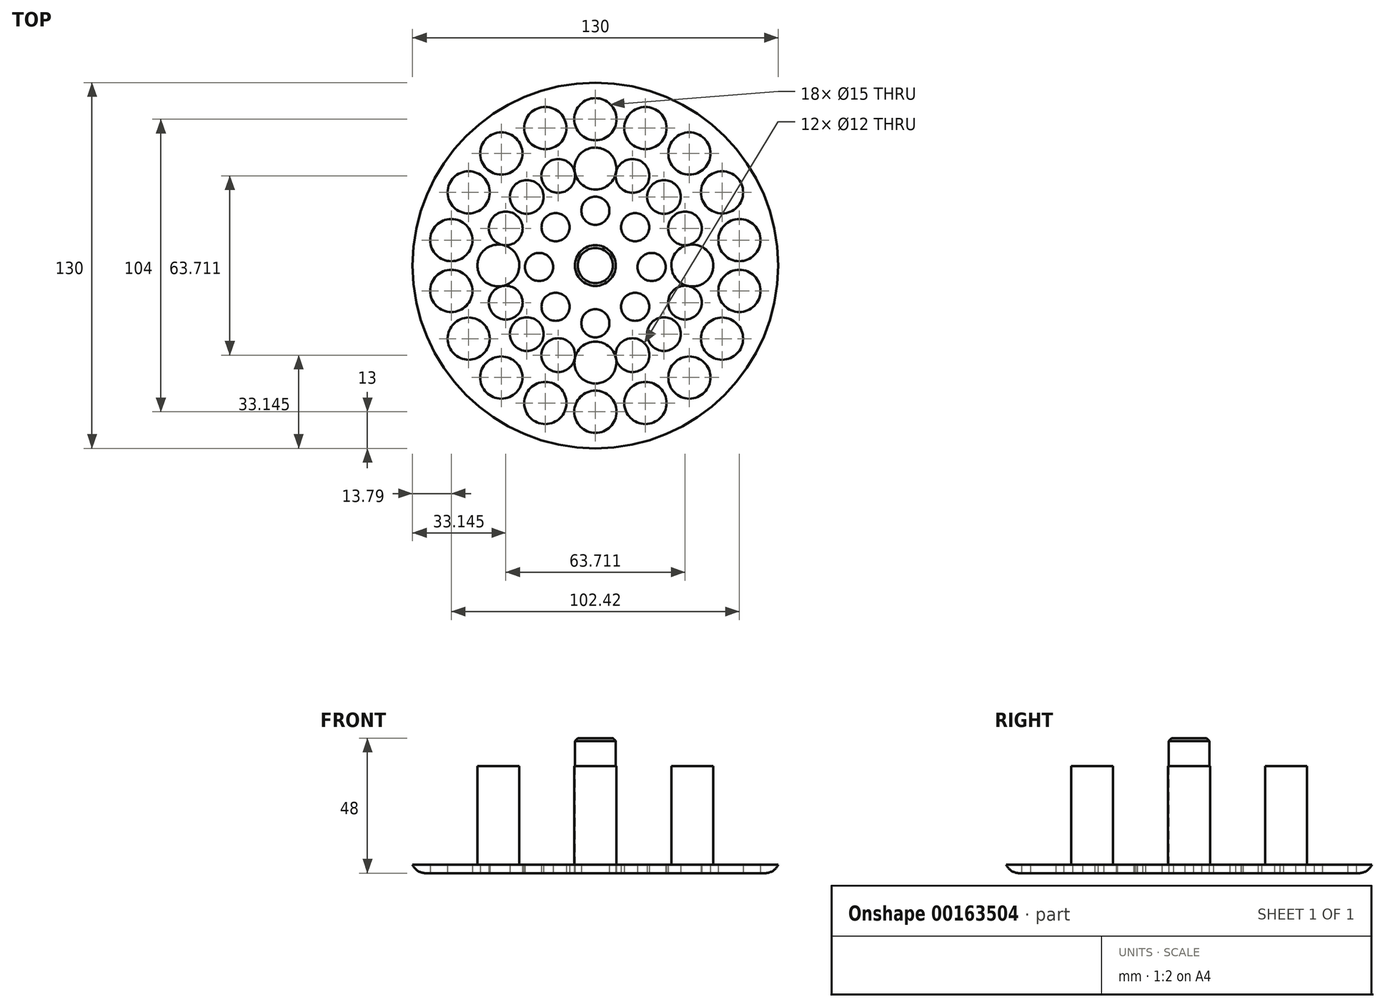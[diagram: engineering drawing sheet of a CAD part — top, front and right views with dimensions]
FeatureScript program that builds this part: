
annotation { "Feature Type Name" : "Feature", "Feature Type Description" : "" }
export const myFeature = defineFeature(function(context is Context, id is Id, definition is map)
    precondition{}
    {
        {
            var Q0;
            Q0=qCreatedBy(makeId("Top.planeOp"),FACE);
            var sketch = newSketch(context, id + "F0", { "sketchPlane" : qUnion([Q0])});
            skCircle(sketch, "E0", {"center": v(0, 0) * mm, "radius": 65 * mm});
            skCircle(sketch, "E1", {"center": v(0, 19.48) * mm, "radius": 5 * mm});
            skCircle(sketch, "E2.1.0", {"center": v(-14.14, 13.62) * mm, "radius": 5 * mm});
            skCircle(sketch, "E2.2.0", {"center": v(-20, -0.52) * mm, "radius": 5 * mm});
            skCircle(sketch, "E2.3.0", {"center": v(-14.14, -14.66) * mm, "radius": 5 * mm});
            skCircle(sketch, "E2.4.0", {"center": v(0, -20.52) * mm, "radius": 5 * mm});
            skCircle(sketch, "E2.5.0", {"center": v(14.14, -14.66) * mm, "radius": 5 * mm});
            skCircle(sketch, "E2.6.0", {"center": v(20, -0.52) * mm, "radius": 5 * mm});
            skCircle(sketch, "E2.7.0", {"center": v(14.14, 13.62) * mm, "radius": 5 * mm});
            skPoint(sketch, "E2.center", {"position": v(0, -0.52) * mm});
            skCircle(sketch, "E3", {"center": v(0, 34.48) * mm, "radius": 6 * mm});
            skCircle(sketch, "E4.1.0", {"center": v(-13.2, 31.86) * mm, "radius": 6 * mm});
            skCircle(sketch, "E4.2.0", {"center": v(-24.38, 24.38) * mm, "radius": 6 * mm});
            skCircle(sketch, "E4.3.0", {"center": v(-31.86, 13.2) * mm, "radius": 6 * mm});
            skCircle(sketch, "E4.4.0", {"center": v(-34.48, 0) * mm, "radius": 6 * mm});
            skCircle(sketch, "E4.5.0", {"center": v(-31.86, -13.2) * mm, "radius": 6 * mm});
            skCircle(sketch, "E4.6.0", {"center": v(-24.38, -24.38) * mm, "radius": 6 * mm});
            skCircle(sketch, "E4.7.0", {"center": v(-13.2, -31.86) * mm, "radius": 6 * mm});
            skCircle(sketch, "E4.8.0", {"center": v(0, -34.48) * mm, "radius": 6 * mm});
            skCircle(sketch, "E4.9.0", {"center": v(13.2, -31.86) * mm, "radius": 6 * mm});
            skCircle(sketch, "E4.10.0", {"center": v(24.38, -24.38) * mm, "radius": 6 * mm});
            skCircle(sketch, "E4.11.0", {"center": v(31.86, -13.2) * mm, "radius": 6 * mm});
            skCircle(sketch, "E4.12.0", {"center": v(34.48, 0) * mm, "radius": 6 * mm});
            skCircle(sketch, "E4.13.0", {"center": v(31.86, 13.2) * mm, "radius": 6 * mm});
            skCircle(sketch, "E4.14.0", {"center": v(24.38, 24.38) * mm, "radius": 6 * mm});
            skCircle(sketch, "E4.15.0", {"center": v(13.2, 31.86) * mm, "radius": 6 * mm});
            skCircle(sketch, "E5", {"center": v(0, 52) * mm, "radius": 7.5 * mm});
            skCircle(sketch, "E6.1.0", {"center": v(-17.79, 48.86) * mm, "radius": 7.5 * mm});
            skCircle(sketch, "E6.2.0", {"center": v(-33.42, 39.83) * mm, "radius": 7.5 * mm});
            skCircle(sketch, "E6.3.0", {"center": v(-45.03, 26) * mm, "radius": 7.5 * mm});
            skCircle(sketch, "E6.4.0", {"center": v(-51.21, 9.03) * mm, "radius": 7.5 * mm});
            skCircle(sketch, "E6.5.0", {"center": v(-51.21, -9.03) * mm, "radius": 7.5 * mm});
            skCircle(sketch, "E6.6.0", {"center": v(-45.03, -26) * mm, "radius": 7.5 * mm});
            skCircle(sketch, "E6.7.0", {"center": v(-33.42, -39.83) * mm, "radius": 7.5 * mm});
            skCircle(sketch, "E6.8.0", {"center": v(-17.79, -48.86) * mm, "radius": 7.5 * mm});
            skCircle(sketch, "E6.9.0", {"center": v(0, -52) * mm, "radius": 7.5 * mm});
            skCircle(sketch, "E6.10.0", {"center": v(17.79, -48.86) * mm, "radius": 7.5 * mm});
            skCircle(sketch, "E6.11.0", {"center": v(33.42, -39.83) * mm, "radius": 7.5 * mm});
            skCircle(sketch, "E6.12.0", {"center": v(45.03, -26) * mm, "radius": 7.5 * mm});
            skCircle(sketch, "E6.13.0", {"center": v(51.21, -9.03) * mm, "radius": 7.5 * mm});
            skCircle(sketch, "E6.14.0", {"center": v(51.21, 9.03) * mm, "radius": 7.5 * mm});
            skCircle(sketch, "E6.15.0", {"center": v(45.03, 26) * mm, "radius": 7.5 * mm});
            skCircle(sketch, "E6.16.0", {"center": v(33.42, 39.83) * mm, "radius": 7.5 * mm});
            skCircle(sketch, "E6.17.0", {"center": v(17.79, 48.86) * mm, "radius": 7.5 * mm});
            skSolve(sketch);
        }
        {
            var Q0;
            Q0=makeQuery(id+"F0.imprint","IMPRINT",FACE,{"disambiguationData":[TD([[makeQuery(id+"F0.imprint","IMPRINT",EDGE,{"derivedFrom":sQuery(id+"F0.wireOp",EDGE,"E0")}),1.0]])]});
            extrude(context, id + "F1", {"entities" : qUnion([Q0]), "depth" : 3 * mm});
        }
        {
            var Q0;
            Q0=makeQuery(id+"F1.opExtrude","CAP_FACE",FACE,{"disambiguationData":[OSD([sQuery(id+"F0.wireOp",EDGE,"E0"),sQuery(id+"F0.wireOp",EDGE,"E1"),sQuery(id+"F0.wireOp",EDGE,"E2.1.0"),sQuery(id+"F0.wireOp",EDGE,"E2.2.0"),sQuery(id+"F0.wireOp",EDGE,"E2.3.0"),sQuery(id+"F0.wireOp",EDGE,"E2.4.0"),sQuery(id+"F0.wireOp",EDGE,"E2.5.0"),sQuery(id+"F0.wireOp",EDGE,"E2.6.0"),sQuery(id+"F0.wireOp",EDGE,"E2.7.0"),sQuery(id+"F0.wireOp",EDGE,"E3"),sQuery(id+"F0.wireOp",EDGE,"E4.1.0"),sQuery(id+"F0.wireOp",EDGE,"E4.2.0"),sQuery(id+"F0.wireOp",EDGE,"E4.3.0"),sQuery(id+"F0.wireOp",EDGE,"E4.4.0"),sQuery(id+"F0.wireOp",EDGE,"E4.5.0"),sQuery(id+"F0.wireOp",EDGE,"E4.6.0"),sQuery(id+"F0.wireOp",EDGE,"E4.7.0"),sQuery(id+"F0.wireOp",EDGE,"E4.8.0"),sQuery(id+"F0.wireOp",EDGE,"E4.9.0"),sQuery(id+"F0.wireOp",EDGE,"E4.10.0"),sQuery(id+"F0.wireOp",EDGE,"E4.11.0"),sQuery(id+"F0.wireOp",EDGE,"E4.12.0"),sQuery(id+"F0.wireOp",EDGE,"E4.13.0"),sQuery(id+"F0.wireOp",EDGE,"E4.14.0"),sQuery(id+"F0.wireOp",EDGE,"E4.15.0"),sQuery(id+"F0.wireOp",EDGE,"E5"),sQuery(id+"F0.wireOp",EDGE,"E6.1.0"),sQuery(id+"F0.wireOp",EDGE,"E6.2.0"),sQuery(id+"F0.wireOp",EDGE,"E6.3.0"),sQuery(id+"F0.wireOp",EDGE,"E6.4.0"),sQuery(id+"F0.wireOp",EDGE,"E6.5.0"),sQuery(id+"F0.wireOp",EDGE,"E6.6.0"),sQuery(id+"F0.wireOp",EDGE,"E6.7.0"),sQuery(id+"F0.wireOp",EDGE,"E6.8.0"),sQuery(id+"F0.wireOp",EDGE,"E6.9.0"),sQuery(id+"F0.wireOp",EDGE,"E6.10.0"),sQuery(id+"F0.wireOp",EDGE,"E6.11.0"),sQuery(id+"F0.wireOp",EDGE,"E6.12.0"),sQuery(id+"F0.wireOp",EDGE,"E6.13.0"),sQuery(id+"F0.wireOp",EDGE,"E6.14.0"),sQuery(id+"F0.wireOp",EDGE,"E6.15.0"),sQuery(id+"F0.wireOp",EDGE,"E6.16.0"),sQuery(id+"F0.wireOp",EDGE,"E6.17.0")])],"isStart":false});
            var sketch = newSketch(context, id + "F2", { "sketchPlane" : qUnion([Q0])});
            skCircle(sketch, "E7", {"center": v(0, 0) * mm, "radius": 7.25 * mm});
            skCircle(sketch, "E8", {"center": v(-24.97, 0) * mm, "radius": 1.76 * mm});
            skSolve(sketch);
        }
        {
            var Q0;
            Q0=makeQuery(id+"F2.imprint","IMPRINT",FACE,{"disambiguationData":[TD([[makeQuery(id+"F2.imprint","IMPRINT",EDGE,{"derivedFrom":sQuery(id+"F2.wireOp",EDGE,"E7")}),1.0]])]});
            extrude(context, id + "F3", {"entities" : qUnion([Q0]), "operationType" : NewBodyOperationType.ADD, "depth" : 45 * mm});
        }
        {
            var Q0;
            Q0=makeQuery(id+"F3.opExtrude","CAP_EDGE",EDGE,{"disambiguationData":[OSD([sQuery(id+"F2.wireOp",EDGE,"E7")])],"isStart":false});
            chamfer(context, id + "F4", {"entities" : qUnion([Q0]), "width" : 1 * mm, "tangentPropagation" : true});
        }
        {
            var Q0;
            Q0=makeQuery(id+"F1.opExtrude","CAP_FACE",FACE,{"disambiguationData":[OSD([sQuery(id+"F0.wireOp",EDGE,"E0"),sQuery(id+"F0.wireOp",EDGE,"E1"),sQuery(id+"F0.wireOp",EDGE,"E2.1.0"),sQuery(id+"F0.wireOp",EDGE,"E2.2.0"),sQuery(id+"F0.wireOp",EDGE,"E2.3.0"),sQuery(id+"F0.wireOp",EDGE,"E2.4.0"),sQuery(id+"F0.wireOp",EDGE,"E2.5.0"),sQuery(id+"F0.wireOp",EDGE,"E2.6.0"),sQuery(id+"F0.wireOp",EDGE,"E2.7.0"),sQuery(id+"F0.wireOp",EDGE,"E3"),sQuery(id+"F0.wireOp",EDGE,"E4.1.0"),sQuery(id+"F0.wireOp",EDGE,"E4.2.0"),sQuery(id+"F0.wireOp",EDGE,"E4.3.0"),sQuery(id+"F0.wireOp",EDGE,"E4.4.0"),sQuery(id+"F0.wireOp",EDGE,"E4.5.0"),sQuery(id+"F0.wireOp",EDGE,"E4.6.0"),sQuery(id+"F0.wireOp",EDGE,"E4.7.0"),sQuery(id+"F0.wireOp",EDGE,"E4.8.0"),sQuery(id+"F0.wireOp",EDGE,"E4.9.0"),sQuery(id+"F0.wireOp",EDGE,"E4.10.0"),sQuery(id+"F0.wireOp",EDGE,"E4.11.0"),sQuery(id+"F0.wireOp",EDGE,"E4.12.0"),sQuery(id+"F0.wireOp",EDGE,"E4.13.0"),sQuery(id+"F0.wireOp",EDGE,"E4.14.0"),sQuery(id+"F0.wireOp",EDGE,"E4.15.0"),sQuery(id+"F0.wireOp",EDGE,"E5"),sQuery(id+"F0.wireOp",EDGE,"E6.1.0"),sQuery(id+"F0.wireOp",EDGE,"E6.2.0"),sQuery(id+"F0.wireOp",EDGE,"E6.3.0"),sQuery(id+"F0.wireOp",EDGE,"E6.4.0"),sQuery(id+"F0.wireOp",EDGE,"E6.5.0"),sQuery(id+"F0.wireOp",EDGE,"E6.6.0"),sQuery(id+"F0.wireOp",EDGE,"E6.7.0"),sQuery(id+"F0.wireOp",EDGE,"E6.8.0"),sQuery(id+"F0.wireOp",EDGE,"E6.9.0"),sQuery(id+"F0.wireOp",EDGE,"E6.10.0"),sQuery(id+"F0.wireOp",EDGE,"E6.11.0"),sQuery(id+"F0.wireOp",EDGE,"E6.12.0"),sQuery(id+"F0.wireOp",EDGE,"E6.13.0"),sQuery(id+"F0.wireOp",EDGE,"E6.14.0"),sQuery(id+"F0.wireOp",EDGE,"E6.15.0"),sQuery(id+"F0.wireOp",EDGE,"E6.16.0"),sQuery(id+"F0.wireOp",EDGE,"E6.17.0")])],"isStart":false});
            var sketch = newSketch(context, id + "F5", { "sketchPlane" : qUnion([Q0])});
            skCircle(sketch, "E9", {"center": v(0, 34.48) * mm, "radius": 7.45 * mm});
            skCircle(sketch, "E10.1.0", {"center": v(-34.48, 0) * mm, "radius": 7.45 * mm});
            skCircle(sketch, "E10.2.0", {"center": v(0, -34.48) * mm, "radius": 7.45 * mm});
            skCircle(sketch, "E10.3.0", {"center": v(34.48, 0) * mm, "radius": 7.45 * mm});
            skPoint(sketch, "E10.center", {"position": v(0, 0) * mm});
            skSolve(sketch);
        }
        {
            var Q0;
            Q0=makeQuery(id+"F5.imprint","IMPRINT",FACE,{"disambiguationData":[TD([[makeQuery(id+"F5.imprint","IMPRINT",EDGE,{"derivedFrom":makeQuery(id+"F1.opExtrude","CAP_EDGE",EDGE,{"disambiguationData":[OSD([sQuery(id+"F0.wireOp",EDGE,"E4.4.0")])],"isStart":false})}),1.0]])]});
            var Q1;
            Q1=makeQuery(id+"F5.imprint","IMPRINT",FACE,{"disambiguationData":[TD([[makeQuery(id+"F5.imprint","IMPRINT",EDGE,{"derivedFrom":makeQuery(id+"F1.opExtrude","CAP_EDGE",EDGE,{"disambiguationData":[OSD([sQuery(id+"F0.wireOp",EDGE,"E4.8.0")])],"isStart":false})}),1.0]])]});
            var Q2;
            Q2=makeQuery(id+"F5.imprint","IMPRINT",FACE,{"disambiguationData":[TD([[makeQuery(id+"F5.imprint","IMPRINT",EDGE,{"derivedFrom":makeQuery(id+"F1.opExtrude","CAP_EDGE",EDGE,{"disambiguationData":[OSD([sQuery(id+"F0.wireOp",EDGE,"E4.12.0")])],"isStart":false})}),1.0]])]});
            var Q3;
            Q3=makeQuery(id+"F5.imprint","IMPRINT",FACE,{"disambiguationData":[TD([[makeQuery(id+"F5.imprint","IMPRINT",EDGE,{"derivedFrom":makeQuery(id+"F1.opExtrude","CAP_EDGE",EDGE,{"disambiguationData":[OSD([sQuery(id+"F0.wireOp",EDGE,"E3")])],"isStart":false})}),-1.0]])]});
            var Q4;
            Q4=makeQuery(id+"F5.imprint","IMPRINT",FACE,{"disambiguationData":[TD([[makeQuery(id+"F5.imprint","IMPRINT",EDGE,{"derivedFrom":makeQuery(id+"F1.opExtrude","CAP_EDGE",EDGE,{"disambiguationData":[OSD([sQuery(id+"F0.wireOp",EDGE,"E4.4.0")])],"isStart":false})}),-1.0]])]});
            var Q5;
            Q5=makeQuery(id+"F5.imprint","IMPRINT",FACE,{"disambiguationData":[TD([[makeQuery(id+"F5.imprint","IMPRINT",EDGE,{"derivedFrom":makeQuery(id+"F1.opExtrude","CAP_EDGE",EDGE,{"disambiguationData":[OSD([sQuery(id+"F0.wireOp",EDGE,"E4.8.0")])],"isStart":false})}),-1.0]])]});
            var Q6;
            Q6=makeQuery(id+"F5.imprint","IMPRINT",FACE,{"disambiguationData":[TD([[makeQuery(id+"F5.imprint","IMPRINT",EDGE,{"derivedFrom":makeQuery(id+"F1.opExtrude","CAP_EDGE",EDGE,{"disambiguationData":[OSD([sQuery(id+"F0.wireOp",EDGE,"E4.12.0")])],"isStart":false})}),-1.0]])]});
            var Q7;
            Q7=makeQuery(id+"F5.imprint","IMPRINT",FACE,{"disambiguationData":[TD([[makeQuery(id+"F5.imprint","IMPRINT",EDGE,{"derivedFrom":makeQuery(id+"F1.opExtrude","CAP_EDGE",EDGE,{"disambiguationData":[OSD([sQuery(id+"F0.wireOp",EDGE,"E3")])],"isStart":false})}),1.0]])]});
            extrude(context, id + "F6", {"entities" : qUnion([Q0, Q1, Q2, Q3, Q4, Q5, Q6, Q7]), "operationType" : NewBodyOperationType.ADD, "depth" : 35 * mm});
        }
        {
            var Q0;
            Q0=makeQuery(id+"F6.opExtrude","CAP_FACE",FACE,{"disambiguationData":[OSD([sQuery(id+"F5.wireOp",EDGE,"E10.1.0")])],"isStart":true});
            var Q1;
            Q1=makeQuery(id+"F6.opExtrude","CAP_FACE",FACE,{"disambiguationData":[OSD([sQuery(id+"F5.wireOp",EDGE,"E10.2.0")])],"isStart":true});
            var Q2;
            Q2=makeQuery(id+"F6.opExtrude","CAP_FACE",FACE,{"disambiguationData":[OSD([sQuery(id+"F5.wireOp",EDGE,"E10.3.0")])],"isStart":true});
            var Q3;
            Q3=makeQuery(id+"F6.opExtrude","CAP_FACE",FACE,{"disambiguationData":[OSD([sQuery(id+"F5.wireOp",EDGE,"E9")])],"isStart":true});
            var Q4;
            Q4=makeQuery(id+"F1.opExtrude","CAP_FACE",FACE,{"disambiguationData":[OSD([sQuery(id+"F0.wireOp",EDGE,"E0"),sQuery(id+"F0.wireOp",EDGE,"E1"),sQuery(id+"F0.wireOp",EDGE,"E2.1.0"),sQuery(id+"F0.wireOp",EDGE,"E2.2.0"),sQuery(id+"F0.wireOp",EDGE,"E2.3.0"),sQuery(id+"F0.wireOp",EDGE,"E2.4.0"),sQuery(id+"F0.wireOp",EDGE,"E2.5.0"),sQuery(id+"F0.wireOp",EDGE,"E2.6.0"),sQuery(id+"F0.wireOp",EDGE,"E2.7.0"),sQuery(id+"F0.wireOp",EDGE,"E3"),sQuery(id+"F0.wireOp",EDGE,"E4.1.0"),sQuery(id+"F0.wireOp",EDGE,"E4.2.0"),sQuery(id+"F0.wireOp",EDGE,"E4.3.0"),sQuery(id+"F0.wireOp",EDGE,"E4.4.0"),sQuery(id+"F0.wireOp",EDGE,"E4.5.0"),sQuery(id+"F0.wireOp",EDGE,"E4.6.0"),sQuery(id+"F0.wireOp",EDGE,"E4.7.0"),sQuery(id+"F0.wireOp",EDGE,"E4.8.0"),sQuery(id+"F0.wireOp",EDGE,"E4.9.0"),sQuery(id+"F0.wireOp",EDGE,"E4.10.0"),sQuery(id+"F0.wireOp",EDGE,"E4.11.0"),sQuery(id+"F0.wireOp",EDGE,"E4.12.0"),sQuery(id+"F0.wireOp",EDGE,"E4.13.0"),sQuery(id+"F0.wireOp",EDGE,"E4.14.0"),sQuery(id+"F0.wireOp",EDGE,"E4.15.0"),sQuery(id+"F0.wireOp",EDGE,"E5"),sQuery(id+"F0.wireOp",EDGE,"E6.1.0"),sQuery(id+"F0.wireOp",EDGE,"E6.2.0"),sQuery(id+"F0.wireOp",EDGE,"E6.3.0"),sQuery(id+"F0.wireOp",EDGE,"E6.4.0"),sQuery(id+"F0.wireOp",EDGE,"E6.5.0"),sQuery(id+"F0.wireOp",EDGE,"E6.6.0"),sQuery(id+"F0.wireOp",EDGE,"E6.7.0"),sQuery(id+"F0.wireOp",EDGE,"E6.8.0"),sQuery(id+"F0.wireOp",EDGE,"E6.9.0"),sQuery(id+"F0.wireOp",EDGE,"E6.10.0"),sQuery(id+"F0.wireOp",EDGE,"E6.11.0"),sQuery(id+"F0.wireOp",EDGE,"E6.12.0"),sQuery(id+"F0.wireOp",EDGE,"E6.13.0"),sQuery(id+"F0.wireOp",EDGE,"E6.14.0"),sQuery(id+"F0.wireOp",EDGE,"E6.15.0"),sQuery(id+"F0.wireOp",EDGE,"E6.16.0"),sQuery(id+"F0.wireOp",EDGE,"E6.17.0")])],"isStart":true});
            extrude(context, id + "F7", {"entities" : qUnion([Q0, Q1, Q2, Q3]), "operationType" : NewBodyOperationType.ADD, "endBound" : BoundingType.UP_TO_SURFACE, "endBoundEntityFace" : qUnion([Q4]), "depth" : 25 * mm});
        }
        {
            var Q0;
            Q0=makeQuery(id+"F1.opExtrude","CAP_EDGE",EDGE,{"disambiguationData":[OSD([sQuery(id+"F0.wireOp",EDGE,"E0")])],"isStart":true});
            fillet(context, id + "F8", {"entities" : qUnion([Q0]), "radius" : 5 * mm, "tangentPropagation" : true, "allowEdgeOverflow" : false});
        }
    });
